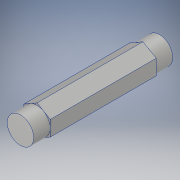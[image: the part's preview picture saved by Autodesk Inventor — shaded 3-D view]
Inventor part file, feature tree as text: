
AUTODESK INVENTOR PART (.ipt)
format: ipt  version: 2019 (Build 230136000, 136)  size: 134,144 bytes
history: native  units: in
note: dims shown in document units (in); Inventor stores cm internally (conversion verified against a paired STEP export)
features: extrude x2, sketch x2, mirror x1, projected_geometry x1
ambient origin geometry x8: Origin, YZ Plane, XZ Plane, XY Plane, X Axis, Y Axis, Z Axis, Center Point
bodies: Solid1 (feature_tree)
feature tree (6):
  extrude  "Extrusion1"  TaperAngle=0.0deg  [1 undecoded]
  extrude  "Extrusion2"  [1 undecoded]
  mirror  "Mirror1"
  sketch  "Sketch1"  dims[d2=0.0in d4=0.0in]
  sketch  "Sketch2"
  projected_geometry  "Projected Loop1"
note: 2 required parameter values undecoded (feature->parameter linkage not recoverable at this tier; creation-order binding heuristic only, values carry confidence <= 0.55)
